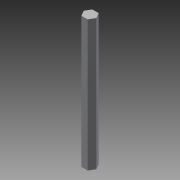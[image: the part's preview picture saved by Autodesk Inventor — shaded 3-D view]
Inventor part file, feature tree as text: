
AUTODESK INVENTOR PART (.ipt)
format: ipt  version: 2014 SP1 (Build 180222100, 222)  size: 72,704 bytes
history: native  units: in
note: dims shown in document units (in); Inventor stores cm internally (conversion verified against a paired STEP export)
features: extrude x1, sketch x1
ambient origin geometry x8: Origin, YZ Plane, XZ Plane, XY Plane, X Axis, Y Axis, Z Axis, Center Point
bodies: Solid1 (feature_tree)
feature tree (2):
  extrude  "Extrusion1"  Depth=6.0in TaperAngle=0.0deg
  sketch  "Sketch1"  dims[d0=0.5in d1=6.0in d2=0.0in]
